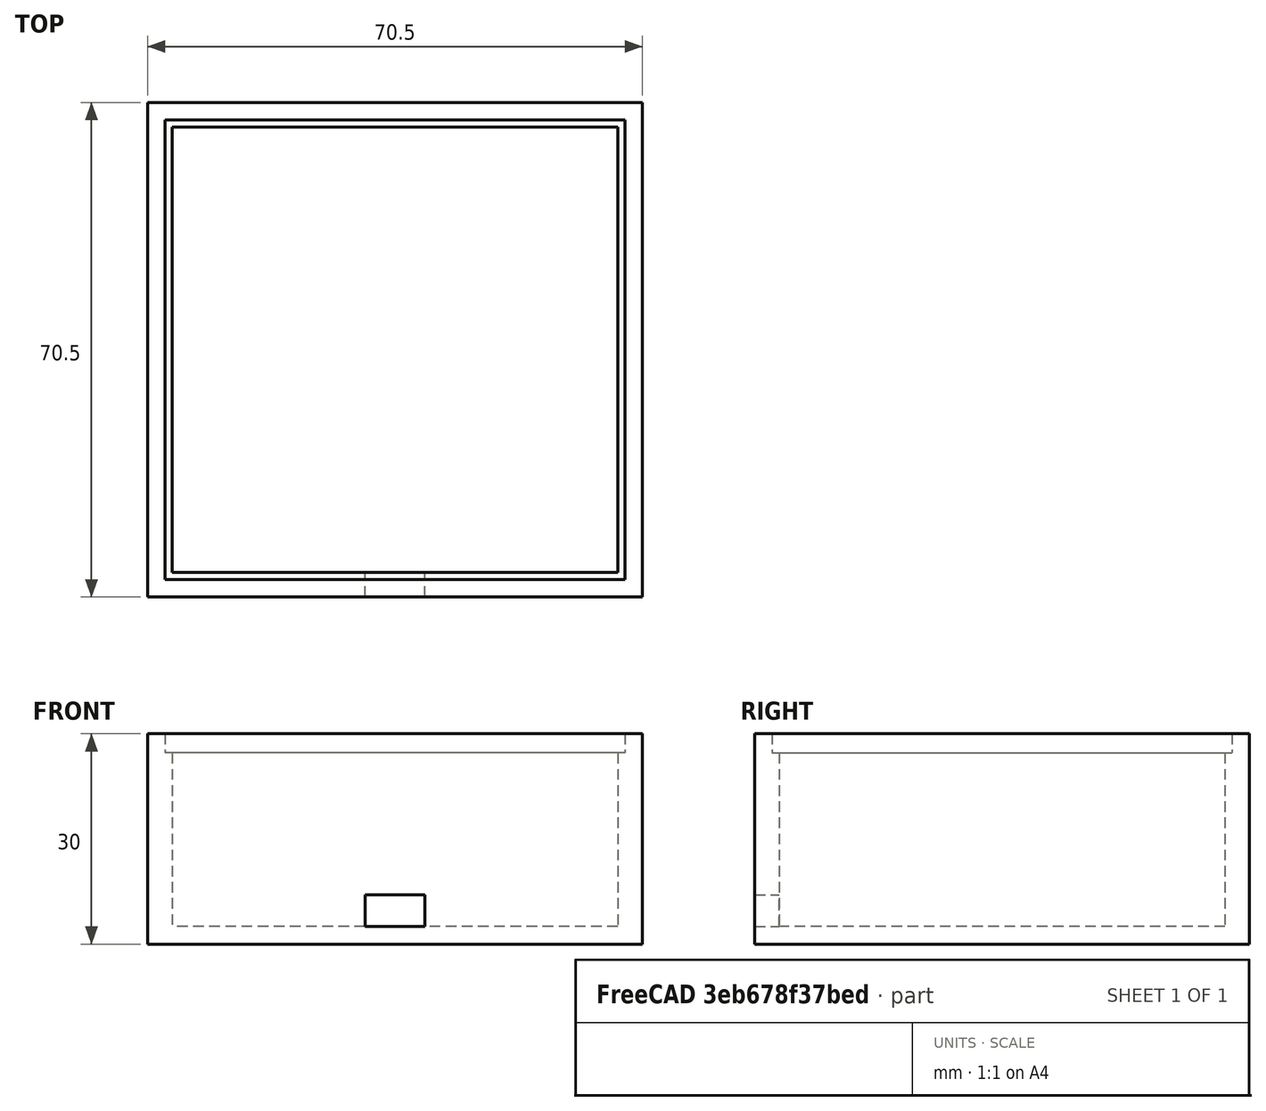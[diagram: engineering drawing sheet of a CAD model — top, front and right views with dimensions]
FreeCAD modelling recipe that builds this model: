
FCSTD DOCUMENT  (FreeCAD 0.19R)
Label: base
License: All rights reserved
LicenseURL: http://en.wikipedia.org/wiki/All_rights_reserved
objects: Sketcher::SketchObject×4, PartDesign::Pocket×3, PartDesign::Pad×1, PartDesign::Body×1, Mesh::Feature×1
note: 13 computed .brp shape members not serialized (recipe doc carries the construction recipe); baked Part::Feature solids carry a one-line shape summary decoded from their .brp

FEATURE [Sketcher::SketchObject] Sketch
  FullyConstrained = true
  MapMode = 5
  Support = -> [XY_Plane]
  sketch-geometry (4):
    g0: LineSegment StartX=0 StartY=0 StartZ=0 EndX=70.5 EndY=0 EndZ=0
    g1: LineSegment StartX=70.5 StartY=0 StartZ=0 EndX=70.5 EndY=70.5 EndZ=0
    g2: LineSegment StartX=70.5 StartY=70.5 StartZ=0 EndX=0 EndY=70.5 EndZ=0
    g3: LineSegment StartX=0 StartY=70.5 StartZ=0 EndX=0 EndY=0 EndZ=0
  constraints (11):
    c: Coincident(g0,g1)
    c: Coincident(g1,g2)
    c: Coincident(g2,g3)
    c: Coincident(g3,g0)
    c: Horizontal(g0)
    c: Horizontal(g2)
    c: Vertical(g1)
    c: Vertical(g3)
    c: Coincident(g0,g-1)
    c: DistanceX(g2,g2) = 70.5
    c: DistanceY(g1,g1) = 70.5
FEATURE [PartDesign::Pad] Pad
  Direction = (1,1,1)
  Length = 30
  Length2 = 100
  Profile = -> Sketch
  Type = 0
FEATURE [Sketcher::SketchObject] Sketch001
  FullyConstrained = true
  MapMode = 5
  Placement = pos=(0,0,30) rot=(0,0,1;0rad)
  Support = -> [Pad]
  sketch-geometry (8):
    g0: LineSegment StartX=3.5 StartY=67 StartZ=0 EndX=67 EndY=67 EndZ=0
    g1: LineSegment StartX=67 StartY=67 StartZ=0 EndX=67 EndY=3.5 EndZ=0
    g2: LineSegment StartX=67 StartY=3.5 StartZ=0 EndX=3.5 EndY=3.5 EndZ=0
    g3: LineSegment StartX=3.5 StartY=3.5 StartZ=0 EndX=3.5 EndY=67 EndZ=0
    g4: LineSegment StartX=0 StartY=0 StartZ=0 EndX=70.5 EndY=0 EndZ=0
    g5: LineSegment StartX=70.5 StartY=0 StartZ=0 EndX=70.5 EndY=70.5 EndZ=0
    g6: LineSegment StartX=70.5 StartY=70.5 StartZ=0 EndX=0 EndY=70.5 EndZ=0
    g7: LineSegment StartX=0 StartY=70.5 StartZ=0 EndX=0 EndY=0 EndZ=0
  constraints (23):
    c: Coincident(g0,g1)
    c: Coincident(g1,g2)
    c: Coincident(g2,g3)
    c: Coincident(g3,g0)
    c: Horizontal(g0)
    c: Horizontal(g2)
    c: Vertical(g1)
    c: Vertical(g3)
    c: Coincident(g4,g5)
    c: Coincident(g5,g6)
    c: Coincident(g6,g7)
    c: Coincident(g7,g4)
    c: Horizontal(g4)
    c: Horizontal(g6)
    c: Vertical(g5)
    c: Vertical(g7)
    c: Coincident(g4,g-1)
    c: DistanceX(g6,g6) = 70.5
    c: DistanceY(g5,g5) = 70.5
    c: DistanceX(g6,g0) = 3.5
    c: DistanceX(g0,g5) = 3.5
    c: DistanceY(g0,g5) = 3.5
    c: DistanceY(g4,g1) = 3.5
FEATURE [PartDesign::Pocket] Pocket
  BaseFeature = -> Pad
  Length = 27.5
  Length2 = 100
  Profile = -> Sketch001
  Type = 0
FEATURE [Sketcher::SketchObject] Sketch002
  FullyConstrained = true
  MapMode = 5
  Placement = pos=(0,0,30) rot=(0,0,1;0rad)
  Support = -> [Pocket]
  sketch-geometry (8):
    g0: LineSegment StartX=0 StartY=0 StartZ=0 EndX=70.5 EndY=0 EndZ=0
    g1: LineSegment StartX=70.5 StartY=0 StartZ=0 EndX=70.5 EndY=70.5 EndZ=0
    g2: LineSegment StartX=70.5 StartY=70.5 StartZ=0 EndX=0 EndY=70.5 EndZ=0
    g3: LineSegment StartX=0 StartY=70.5 StartZ=0 EndX=0 EndY=0 EndZ=0
    g4: LineSegment StartX=2.5 StartY=68 StartZ=0 EndX=68 EndY=68 EndZ=0
    g5: LineSegment StartX=68 StartY=68 StartZ=0 EndX=68 EndY=2.5 EndZ=0
    g6: LineSegment StartX=68 StartY=2.5 StartZ=0 EndX=2.5 EndY=2.5 EndZ=0
    g7: LineSegment StartX=2.5 StartY=2.5 StartZ=0 EndX=2.5 EndY=68 EndZ=0
  constraints (23):
    c: Coincident(g0,g1)
    c: Coincident(g1,g2)
    c: Coincident(g2,g3)
    c: Coincident(g3,g0)
    c: Horizontal(g0)
    c: Horizontal(g2)
    c: Vertical(g1)
    c: Vertical(g3)
    c: Coincident(g0,g-1)
    c: DistanceX(g2,g2) = 70.5
    c: DistanceY(g1,g1) = 70.5
    c: Coincident(g4,g5)
    c: Coincident(g5,g6)
    c: Coincident(g6,g7)
    c: Coincident(g7,g4)
    c: Horizontal(g4)
    c: Horizontal(g6)
    c: Vertical(g5)
    c: Vertical(g7)
    c: DistanceX(g2,g4) = 2.5
    c: DistanceX(g4,g1) = 2.5
    c: DistanceY(g4,g1) = 2.5
    c: DistanceY(g0,g5) = 2.5
FEATURE [PartDesign::Pocket] Pocket001
  BaseFeature = -> Pocket
  Length = 2.75
  Length2 = 100
  Profile = -> Sketch002
  Type = 0
FEATURE [Sketcher::SketchObject] Sketch003
  FullyConstrained = true
  MapMode = 5
  Placement = pos=(0,0,0) rot=(1,0,0;1.5708rad)
  Support = -> [Pocket001]
  sketch-geometry (6):
    g0: LineSegment StartX=0 StartY=0 StartZ=0 EndX=70.5 EndY=0 EndZ=0
    g1: LineSegment StartX=35.25 StartY=0 StartZ=0 EndX=35.25 EndY=2.5 EndZ=0
    g2: LineSegment StartX=31 StartY=7 StartZ=0 EndX=39.5 EndY=7 EndZ=0
    g3: LineSegment StartX=39.5 StartY=7 StartZ=0 EndX=39.5 EndY=2.5 EndZ=0
    g4: LineSegment StartX=39.5 StartY=2.5 StartZ=0 EndX=31 EndY=2.5 EndZ=0
    g5: LineSegment StartX=31 StartY=2.5 StartZ=0 EndX=31 EndY=7 EndZ=0
  constraints (17):
    c: Coincident(g0,g-1)
    c: PointOnObject(g0,g-1)
    c: DistanceX(g0,g0) = 70.5
    c: Vertical(g1)
    c: Symmetric(g-1,g0,g1)
    c: Coincident(g2,g3)
    c: Coincident(g3,g4)
    c: Coincident(g4,g5)
    c: Coincident(g5,g2)
    c: Horizontal(g2)
    c: Horizontal(g4)
    c: Vertical(g3)
    c: Vertical(g5)
    c: Symmetric(g4,g3,g1)
    c: DistanceY(g1,g1) = 2.5
    c: DistanceY(g5,g5) = 4.5
    c: DistanceX(g2,g2) = 8.5
FEATURE [PartDesign::Pocket] Pocket002
  BaseFeature = -> Pocket001
  Length = 5
  Length2 = 100
  Profile = -> Sketch003
  Type = 2
FEATURE [PartDesign::Body] Body
  Group = -> [Sketch,Pad,Sketch001,Pocket,Sketch002,Pocket001,Sketch003,Pocket002]
  Origin = -> Origin
  Tip = -> Pocket002
FEATURE [Mesh::Feature] Mesh  label="Body (Meshed)"
